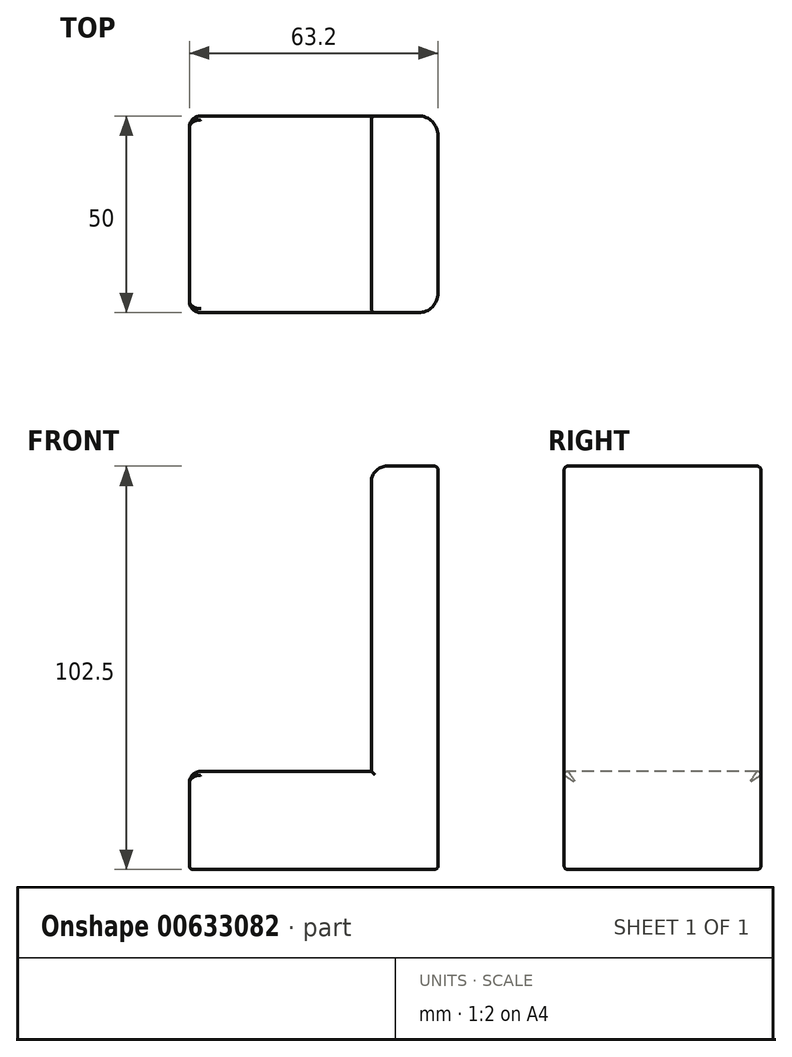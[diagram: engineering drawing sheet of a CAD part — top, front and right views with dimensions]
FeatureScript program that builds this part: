
annotation { "Feature Type Name" : "Feature", "Feature Type Description" : "" }
export const myFeature = defineFeature(function(context is Context, id is Id, definition is map)
    precondition{}
    {
        {
            var Q0;
            Q0=qCreatedBy(makeId("Top.planeOp"),FACE);
            var sketch = newSketch(context, id + "F0", { "sketchPlane" : qUnion([Q0])});
            skLineSegment(sketch, "E0.bottom", {"start": v(25, 25) * mm, "end": v(-25, 25) * mm});
            skLineSegment(sketch, "E0.top", {"start": v(25, -25) * mm, "end": v(-25, -25) * mm});
            skLineSegment(sketch, "E0.left", {"start": v(25, 25) * mm, "end": v(25, -25) * mm});
            skLineSegment(sketch, "E0.right", {"start": v(-25, 25) * mm, "end": v(-25, -25) * mm});
            skPoint(sketch, "E0.middle", {"position": v(0, 0) * mm});
            skSolve(sketch);
        }
        {
            var Q0;
            Q0=makeQuery(id+"F0.imprint","IMPRINT",FACE,{"disambiguationData":[TD([[makeQuery(id+"F0.imprint","IMPRINT",EDGE,{"derivedFrom":sQuery(id+"F0.wireOp",EDGE,"E0.bottom")}),1.0]])]});
            extrude(context, id + "F1", {"entities" : qUnion([Q0]), "depth" : 25 * mm, "offsetDistance" : 25 * mm});
        }
        {
            var Q0;
            Q0=makeQuery(id+"F1.opExtrude","CAP_FACE",FACE,{"disambiguationData":[OSD([sQuery(id+"F0.wireOp",EDGE,"E0.bottom"),sQuery(id+"F0.wireOp",EDGE,"E0.top"),sQuery(id+"F0.wireOp",EDGE,"E0.left"),sQuery(id+"F0.wireOp",EDGE,"E0.right")])],"isStart":true});
            var sketch = newSketch(context, id + "F2", { "sketchPlane" : qUnion([Q0])});
            skLineSegment(sketch, "E1.bottom", {"start": v(20, -20) * mm, "end": v(-20, -20) * mm});
            skLineSegment(sketch, "E1.top", {"start": v(20, 20) * mm, "end": v(-20, 20) * mm});
            skLineSegment(sketch, "E1.left", {"start": v(20, -20) * mm, "end": v(20, 20) * mm});
            skLineSegment(sketch, "E1.right", {"start": v(-20, -20) * mm, "end": v(-20, 20) * mm});
            skPoint(sketch, "E1.middle", {"position": v(0, 0) * mm});
            skSolve(sketch);
        }
        {
            var Q0;
            Q0=makeQuery(id+"F2.imprint","IMPRINT",FACE,{"disambiguationData":[TD([[makeQuery(id+"F2.imprint","IMPRINT",EDGE,{"derivedFrom":sQuery(id+"F2.wireOp",EDGE,"E1.bottom")}),1.0]])]});
            var sketch = newSketch(context, id + "F3", { "sketchPlane" : qUnion([Q0])});
            skCircle(sketch, "E2", {"center": v(-20.07, -19.87) * mm, "radius": 5 * mm});
            skCircle(sketch, "E3", {"center": v(-20.28, 20.07) * mm, "radius": 5 * mm});
            skCircle(sketch, "E4", {"center": v(19.66, -19.66) * mm, "radius": 5 * mm});
            skCircle(sketch, "E5", {"center": v(19.87, 20.07) * mm, "radius": 5 * mm});
            skSolve(sketch);
        }
        {
            var Q0;
            Q0=sQuery(id+"F3.wireOp",EDGE,"E2");
            var Q1;
            Q1=sQuery(id+"F3.wireOp",EDGE,"E3");
            var Q2;
            Q2=sQuery(id+"F3.wireOp",EDGE,"E4");
            var Q3;
            Q3=sQuery(id+"F3.wireOp",EDGE,"E5");
            extrude(context, id + "F4", {"bodyType" : ToolBodyType.SURFACE, "surfaceEntities" : qUnion([Q0, Q1, Q2, Q3]), "depth" : 25 * mm, "offsetDistance" : 25 * mm});
        }
        {
            var Q0;
            Q0=makeQuery(id+"F1.opExtrude","SWEPT_FACE",FACE,{"disambiguationData":[OSD([sQuery(id+"F0.wireOp",EDGE,"E0.left")])]});
            extrude(context, id + "F5", {"entities" : qUnion([Q0]), "operationType" : NewBodyOperationType.ADD, "depth" : 13.2 * mm, "offsetDistance" : 25 * mm});
        }
        {
            var Q0;
            {var subQ0=sQuery(id+"F0.wireOp",EDGE,"E0.left");Q0=makeQuery(id+"F5.boolean.opBoolean","MERGE",FACE,{"derivedFrom":[makeQuery(id+"F1.opExtrude","CAP_FACE",FACE,{"disambiguationData":[OSD([sQuery(id+"F0.wireOp",EDGE,"E0.bottom"),sQuery(id+"F0.wireOp",EDGE,"E0.top"),subQ0,sQuery(id+"F0.wireOp",EDGE,"E0.right")])],"isStart":false}),makeQuery(id+"F5.opExtrude","SWEPT_FACE",FACE,{"disambiguationData":[OSD([subQ0]),TDD([makeQuery(id+"F1.opExtrude","CAP_EDGE",EDGE,{"disambiguationData":[OSD([subQ0])],"isStart":false})])]})]});}
            var sketch = newSketch(context, id + "F6", { "sketchPlane" : qUnion([Q0])});
            skLineSegment(sketch, "E6.bottom", {"start": v(21.23, -25) * mm, "end": v(38.2, -25) * mm});
            skLineSegment(sketch, "E6.top", {"start": v(21.23, 25) * mm, "end": v(38.2, 25) * mm});
            skLineSegment(sketch, "E6.left", {"start": v(21.23, -25) * mm, "end": v(21.23, 25) * mm});
            skLineSegment(sketch, "E6.right", {"start": v(38.2, -25) * mm, "end": v(38.2, 25) * mm});
            skPoint(sketch, "E6.middle", {"position": v(29.71, 0) * mm});
            skSolve(sketch);
        }
        {
            var Q0;
            Q0=makeQuery(id+"F6.imprint","IMPRINT",FACE,{"disambiguationData":[TD([[makeQuery(id+"F6.imprint","IMPRINT",EDGE,{"derivedFrom":sQuery(id+"F6.wireOp",EDGE,"E6.bottom")}),-1.0]])]});
            extrude(context, id + "F7", {"entities" : qUnion([Q0]), "operationType" : NewBodyOperationType.ADD, "depth" : 77.5 * mm, "offsetDistance" : 25 * mm});
        }
        {
            var Q0;
            Q0=makeQuery(id+"F7.opExtrude","SWEPT_FACE",FACE,{"disambiguationData":[OSD([sQuery(id+"F6.wireOp",EDGE,"E6.left")])]});
            var sketch = newSketch(context, id + "F8", { "sketchPlane" : qUnion([Q0])});
            skCircle(sketch, "E7", {"center": v(-21.55, 55.67) * mm, "radius": 3.25 * mm});
            skCircle(sketch, "E8", {"center": v(21.55, 56.54) * mm, "radius": 3.25 * mm});
            skSolve(sketch);
        }
        {
            var Q0;
            Q0=sQuery(id+"F8.wireOp",EDGE,"E7");
            var Q1;
            Q1=sQuery(id+"F8.wireOp",EDGE,"E8");
            extrude(context, id + "F9", {"bodyType" : ToolBodyType.SURFACE, "surfaceEntities" : qUnion([Q0, Q1]), "depth" : 49.3 * mm, "offsetDistance" : 25 * mm});
        }
        {
            var Q0;
            Q0=makeQuery(id+"F7.opExtrude","CAP_EDGE",EDGE,{"disambiguationData":[OSD([sQuery(id+"F6.wireOp",EDGE,"E6.left")])],"isStart":false});
            fillet(context, id + "F10", {"entities" : qUnion([Q0]), "radius" : 4 * mm, "tangentPropagation" : true, "allowEdgeOverflow" : false});
        }
        {
            var Q0;
            Q0=makeQuery(id+"F7.opExtrude","CAP_EDGE",EDGE,{"disambiguationData":[OSD([sQuery(id+"F6.wireOp",EDGE,"E6.right")])],"isStart":false});
            var Q1;
            {var subQ0=sQuery(id+"F0.wireOp",EDGE,"E0.left");Q1=makeQuery(id+"F5.opExtrude","CAP_EDGE",EDGE,{"disambiguationData":[OSD([subQ0]),TDD([makeQuery(id+"F1.opExtrude","CAP_EDGE",EDGE,{"disambiguationData":[OSD([subQ0])],"isStart":true})])],"isStart":false});}
            var Q2;
            Q2=makeQuery(id+"F1.opExtrude","CAP_EDGE",EDGE,{"disambiguationData":[OSD([sQuery(id+"F0.wireOp",EDGE,"E0.right")])],"isStart":true});
            var Q3;
            {var subQ0=sQuery(id+"F0.wireOp",EDGE,"E0.left");var subQ1=sQuery(id+"F0.wireOp",EDGE,"E0.top");Q3=makeQuery(id+"F5.boolean.opBoolean","MERGE",EDGE,{"derivedFrom":[makeQuery(id+"F1.opExtrude","CAP_EDGE",EDGE,{"disambiguationData":[OSD([subQ1])],"isStart":true}),makeQuery(id+"F5.opExtrude","SWEPT_EDGE",EDGE,{"disambiguationData":[OSD([subQ1,subQ0]),TDD([makeQuery(id+"F1.opExtrude","CAP_VERTEX",VERTEX,{"disambiguationData":[OSD([subQ1,subQ0])],"isStart":true})])]})]});}
            var Q4;
            {var subQ0=sQuery(id+"F0.wireOp",EDGE,"E0.left");var subQ1=sQuery(id+"F0.wireOp",EDGE,"E0.bottom");Q4=makeQuery(id+"F5.boolean.opBoolean","MERGE",EDGE,{"derivedFrom":[makeQuery(id+"F1.opExtrude","CAP_EDGE",EDGE,{"disambiguationData":[OSD([subQ1])],"isStart":true}),makeQuery(id+"F5.opExtrude","SWEPT_EDGE",EDGE,{"disambiguationData":[OSD([subQ1,subQ0]),TDD([makeQuery(id+"F1.opExtrude","CAP_VERTEX",VERTEX,{"disambiguationData":[OSD([subQ1,subQ0])],"isStart":true})])]})]});}
            var Q5;
            {var subQ0=sQuery(id+"F0.wireOp",EDGE,"E0.left");var subQ1=sQuery(id+"F0.wireOp",EDGE,"E0.top");Q5=makeQuery(id+"F5.boolean.opBoolean","MERGE",EDGE,{"derivedFrom":[makeQuery(id+"F1.opExtrude","CAP_EDGE",EDGE,{"disambiguationData":[OSD([subQ1])],"isStart":false}),makeQuery(id+"F5.opExtrude","SWEPT_EDGE",EDGE,{"disambiguationData":[OSD([subQ1,subQ0]),TDD([makeQuery(id+"F1.opExtrude","CAP_VERTEX",VERTEX,{"disambiguationData":[OSD([subQ1,subQ0])],"isStart":false})])]})]});}
            var Q6;
            {var subQ0=sQuery(id+"F0.wireOp",EDGE,"E0.left");var subQ1=sQuery(id+"F0.wireOp",EDGE,"E0.bottom");Q6=makeQuery(id+"F5.boolean.opBoolean","MERGE",EDGE,{"derivedFrom":[makeQuery(id+"F1.opExtrude","CAP_EDGE",EDGE,{"disambiguationData":[OSD([subQ1])],"isStart":false}),makeQuery(id+"F5.opExtrude","SWEPT_EDGE",EDGE,{"disambiguationData":[OSD([subQ1,subQ0]),TDD([makeQuery(id+"F1.opExtrude","CAP_VERTEX",VERTEX,{"disambiguationData":[OSD([subQ1,subQ0])],"isStart":false})])]})]});}
            var Q7;
            Q7=makeQuery(id+"F7.opExtrude","SWEPT_EDGE",EDGE,{"disambiguationData":[OSD([sQuery(id+"F0.wireOp",EDGE,"E0.bottom"),sQuery(id+"F0.wireOp",EDGE,"E0.left"),sQuery(id+"F6.wireOp",EDGE,"E6.top"),sQuery(id+"F6.wireOp",EDGE,"E6.left")])]});
            var Q8;
            Q8=makeQuery(id+"F7.opExtrude","SWEPT_EDGE",EDGE,{"disambiguationData":[OSD([sQuery(id+"F0.wireOp",EDGE,"E0.top"),sQuery(id+"F0.wireOp",EDGE,"E0.left"),sQuery(id+"F6.wireOp",EDGE,"E6.bottom"),sQuery(id+"F6.wireOp",EDGE,"E6.left")])]});
            var Q9;
            Q9=makeQuery(id+"F7.opExtrude","CAP_EDGE",EDGE,{"disambiguationData":[OSD([sQuery(id+"F6.wireOp",EDGE,"E6.left")])],"isStart":true});
            fillet(context, id + "F11", {"entities" : qUnion([Q0, Q1, Q2, Q3, Q4, Q5, Q6, Q7, Q8, Q9]), "radius" : 1 * mm, "tangentPropagation" : true, "allowEdgeOverflow" : false});
        }
        {
            var Q0;
            Q0=makeQuery(id+"F1.opExtrude","CAP_EDGE",EDGE,{"disambiguationData":[OSD([sQuery(id+"F0.wireOp",EDGE,"E0.right")])],"isStart":false});
            fillet(context, id + "F12", {"entities" : qUnion([Q0]), "radius" : 3 * mm, "tangentPropagation" : true, "allowEdgeOverflow" : false});
        }
        {
            var Q0;
            Q0=makeQuery(id+"F5.opExtrude","CAP_EDGE",EDGE,{"disambiguationData":[OSD([sQuery(id+"F0.wireOp",EDGE,"E0.bottom"),sQuery(id+"F0.wireOp",EDGE,"E0.left")])],"isStart":false});
            var Q1;
            Q1=makeQuery(id+"F5.opExtrude","CAP_EDGE",EDGE,{"disambiguationData":[OSD([sQuery(id+"F0.wireOp",EDGE,"E0.top"),sQuery(id+"F0.wireOp",EDGE,"E0.left")])],"isStart":false});
            fillet(context, id + "F13", {"entities" : qUnion([Q0, Q1]), "radius" : 5 * mm, "tangentPropagation" : true, "allowEdgeOverflow" : false});
        }
    });
